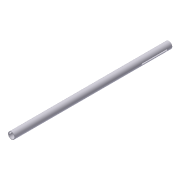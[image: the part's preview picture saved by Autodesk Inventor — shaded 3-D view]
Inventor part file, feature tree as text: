
AUTODESK INVENTOR PART (.ipt)
format: ipt  version: 2012 (Build 160160000, 160)  size: 112,640 bytes
history: native  units: in
note: dims shown in document units (in); Inventor stores cm internally (conversion verified against a paired STEP export)
features: extrude x3, sketch x3, projected_geometry x2, plane x1, other x1
ambient origin geometry x8: Origin, YZ Plane, XZ Plane, XY Plane, X Axis, Y Axis, Z Axis, Center Point
bodies: Solid1 (feature_tree)
feature tree (10):
  extrude  "Extrusion1"  Depth=1.375in
  plane  "Work Plane1"
  extrude  "Extrusion2"  TaperAngle=0.0deg  [1 undecoded]
  extrude  "Extrusion3"  Depth=1.5in
  sketch  "Sketch1"  dims[d0=1.656in d1=1.375in]
  other  "Work Axis1"
  sketch  "Sketch2"  dims[d2=38.0in d3=0.0in d4=0.0in]
  projected_geometry  "Projected Loop1"
  projected_geometry  "Projected Loop2"
  sketch  "Sketch3"  dims[d5=0.3125in d6=1.5in d7=0.25in d8=38.0in d9=0.0in d10=0.25in d11=0.25in d12=0.125in d13=0.25in d14=6.0in d15=1.25in d16=38.0in d17=0.0in d18=0.5in d19=0.5in]
note: 1 required parameter value undecoded (feature->parameter linkage not recoverable at this tier; creation-order binding heuristic only, values carry confidence <= 0.55)
